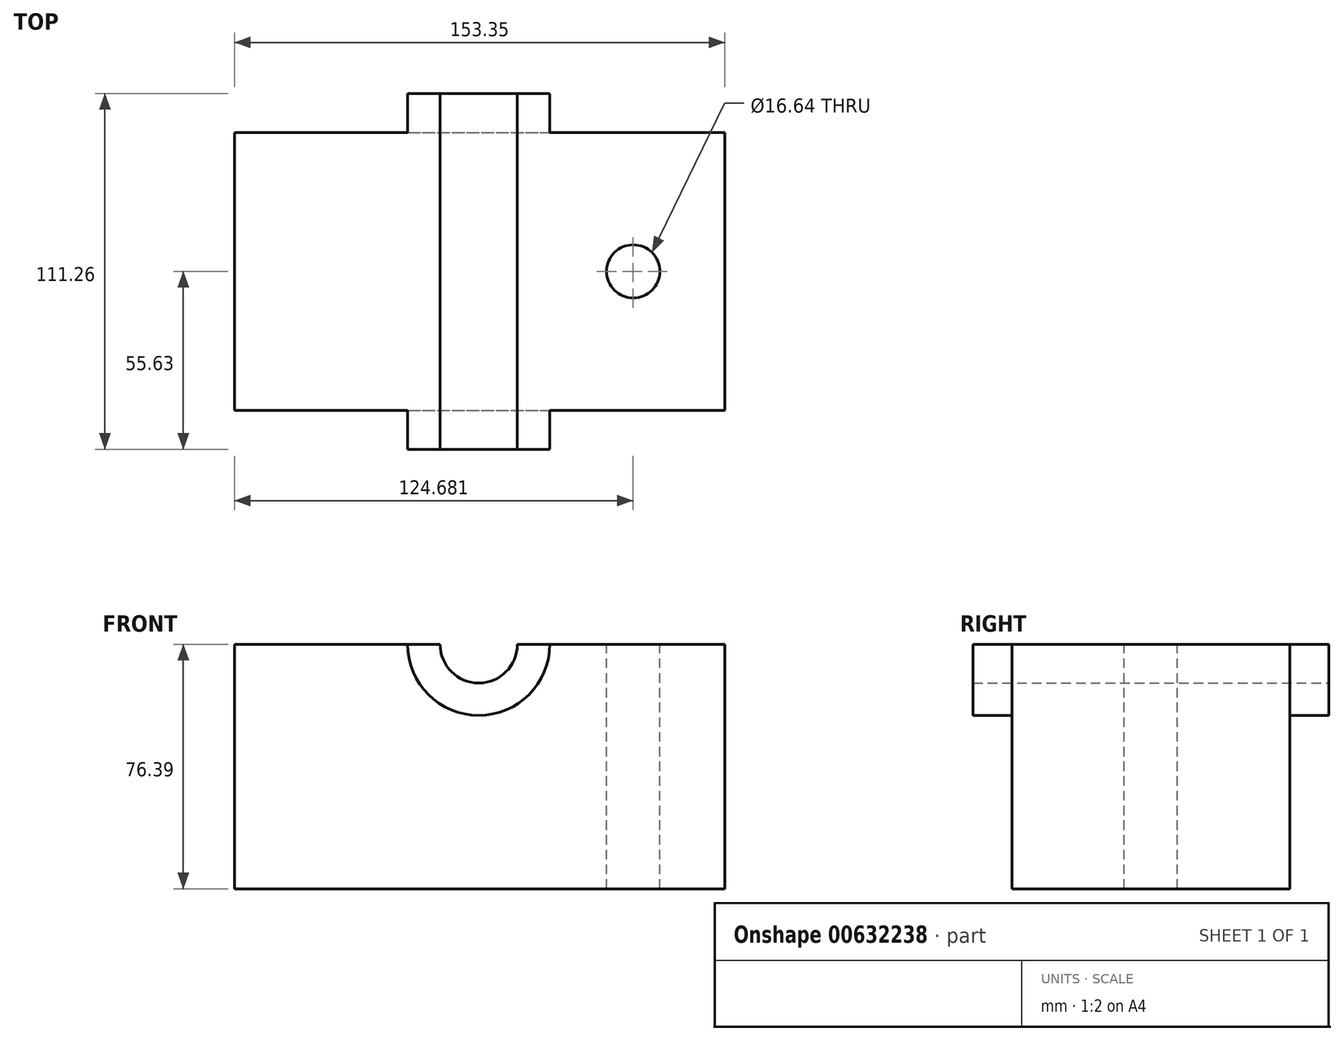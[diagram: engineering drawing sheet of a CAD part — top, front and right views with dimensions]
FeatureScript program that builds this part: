
annotation { "Feature Type Name" : "Feature", "Feature Type Description" : "" }
export const myFeature = defineFeature(function(context is Context, id is Id, definition is map)
    precondition{}
    {
        {
            var Q0;
            Q0=qCreatedBy(makeId("Front.planeOp"),FACE);
            var sketch = newSketch(context, id + "F0", { "sketchPlane" : qUnion([Q0])});
            skArc(sketch, "E0", {"start": v(-12.08, 0) * mm, "mid": v(0, -12.08) * mm, "end": v(12.08, 0) * mm});
            skArc(sketch, "E1", {"start": v(-22.21, 0) * mm, "mid": v(0, -22.21) * mm, "end": v(22.21, 0) * mm});
            skLineSegment(sketch, "E2.bottom", {"start": v(-76.4, 0) * mm, "end": v(-12.08, 0) * mm});
            skLineSegment(sketch, "E2.top", {"start": v(-76.4, -76.4) * mm, "end": v(76.96, -76.4) * mm});
            skLineSegment(sketch, "E2.left", {"start": v(-76.4, 0) * mm, "end": v(-76.4, -76.4) * mm});
            skLineSegment(sketch, "E2.right", {"start": v(76.96, 0) * mm, "end": v(76.96, -76.4) * mm});
            skLineSegment(sketch, "E3.trimOffspring", {"start": v(12.08, 0) * mm, "end": v(76.96, 0) * mm});
            skSolve(sketch);
        }
        {
            var Q0;
            {var subQ2=sQuery(id+"F0.wireOp",EDGE,"E1");Q0=makeQuery(id+"F0.imprint","IMPRINT",FACE,{"disambiguationData":[TD([[makeQuery(id+"F0.imprint","IMPRINT",EDGE,{"derivedFrom":subQ2}),-1.0]])]});}
            extrude(context, id + "F1", {"entities" : qUnion([Q0]), "endBound" : BoundingType.SYMMETRIC, "depth" : 86.87 * mm, "offsetDistance" : 25.4 * mm});
        }
        {
            var Q0;
            {var subQ0=sQuery(id+"F0.wireOp",EDGE,"E0");Q0=makeQuery(id+"F0.imprint","IMPRINT",FACE,{"disambiguationData":[TD([[makeQuery(id+"F0.imprint","IMPRINT",EDGE,{"derivedFrom":subQ0}),-1.0]])]});}
            extrude(context, id + "F2", {"entities" : qUnion([Q0]), "operationType" : NewBodyOperationType.ADD, "endBound" : BoundingType.SYMMETRIC, "depth" : 111.25 * mm, "offsetDistance" : 25.4 * mm});
        }
        {
            var Q0;
            {var subQ0=sQuery(id+"F0.wireOp",EDGE,"E3.trimOffspring");Q0=makeQuery(id+"F2.boolean.opBoolean","MERGE",FACE,{"derivedFrom":[makeQuery(id+"F1.opExtrude","SWEPT_FACE",FACE,{"disambiguationData":[OSD([subQ0])]}),makeQuery(id+"F2.opExtrude","SWEPT_FACE",FACE,{"disambiguationData":[OSD([subQ0])]})]});}
            var sketch = newSketch(context, id + "F3", { "sketchPlane" : qUnion([Q0])});
            skCircle(sketch, "E4", {"center": v(48.3, 0) * mm, "radius": 8.32 * mm});
            skSolve(sketch);
        }
        {
            var Q0;
            Q0 = qSketchRegion(id + "F3", true);
            extrude(context, id + "F4", {"entities" : qUnion([Q0]), "operationType" : NewBodyOperationType.REMOVE, "endBound" : BoundingType.THROUGH_ALL, "oppositeDirection" : true, "depth" : 25.4 * mm, "offsetDistance" : 25.4 * mm});
        }
    });
